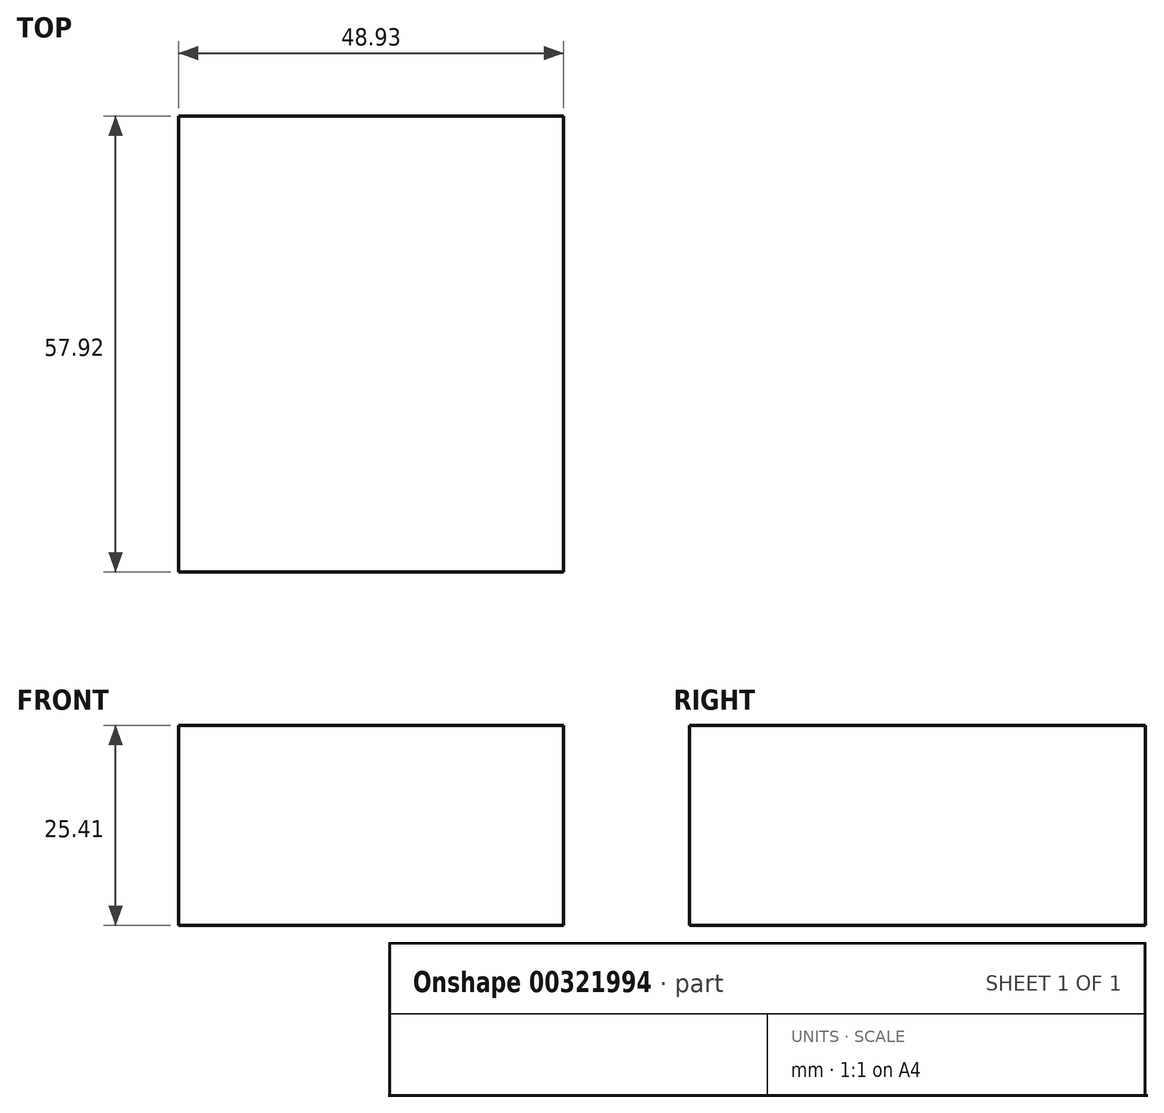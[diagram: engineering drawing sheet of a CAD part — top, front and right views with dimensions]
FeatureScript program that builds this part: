
annotation { "Feature Type Name" : "Feature", "Feature Type Description" : "" }
export const myFeature = defineFeature(function(context is Context, id is Id, definition is map)
    precondition{}
    {
        {
            var Q0;
            Q0=qCreatedBy(makeId("Front.planeOp"),FACE);
            var sketch = newSketch(context, id + "F0", { "sketchPlane" : qUnion([Q0])});
            skLineSegment(sketch, "E0.rect.bottom", {"start": v(-41.28, 9.52) * mm, "end": v(41.28, 9.52) * mm});
            skLineSegment(sketch, "E0.rect.top", {"start": v(-41.28, -9.52) * mm, "end": v(41.28, -9.52) * mm});
            skLineSegment(sketch, "E0.rect.left", {"start": v(-41.28, 9.52) * mm, "end": v(-41.28, -9.52) * mm});
            skLineSegment(sketch, "E0.rect.right", {"start": v(41.28, 9.52) * mm, "end": v(41.28, -9.52) * mm});
            skPoint(sketch, "E0.rect.middle", {"position": v(0, 0) * mm});
            skLineSegment(sketch, "E1", {"start": v(41.28, 9.52) * mm, "end": v(41.28, 27) * mm});
            skArc(sketch, "E2", {"start": v(41.28, 27) * mm, "mid": v(45.92, 38.23) * mm, "end": v(57.15, 42.88) * mm});
            skLineSegment(sketch, "E3", {"start": v(57.15, 42.88) * mm, "end": v(85.72, 42.88) * mm});
            skLineSegment(sketch, "E4.rect.bottom", {"start": v(60.32, 38.1) * mm, "end": v(111.12, 38.1) * mm});
            skLineSegment(sketch, "E4.rect.top", {"start": v(60.32, 66.68) * mm, "end": v(111.12, 66.68) * mm});
            skLineSegment(sketch, "E4.rect.left", {"start": v(60.32, 38.1) * mm, "end": v(60.32, 66.68) * mm});
            skLineSegment(sketch, "E4.rect.right", {"start": v(111.13, 38.1) * mm, "end": v(111.12, 66.68) * mm});
            skPoint(sketch, "E4.rect.middle", {"position": v(85.72, 52.39) * mm});
            skLineSegment(sketch, "E5.0", {"start": v(57.15, 61.93) * mm, "end": v(85.72, 61.93) * mm});
            skArc(sketch, "E5.1", {"start": v(22.23, 27) * mm, "mid": v(32.45, 51.7) * mm, "end": v(57.15, 61.93) * mm});
            skLineSegment(sketch, "E5.2", {"start": v(22.23, 9.52) * mm, "end": v(22.23, 27) * mm});
            skLineSegment(sketch, "E6", {"start": v(85.72, 38.1) * mm, "end": v(85.72, 66.68) * mm});
            skFitSpline(sketch, "E7", {"points": [v(-41.28, 9.53) * mm, v(57.15, 61.93) * mm], "startDerivative": vector(5.2, 92.34) * mm, "endDerivative": vector(120.92, 4.22) * mm});
            skSolve(sketch);
        }
        {
            var Q0;
            Q0=makeQuery(id+"F0.imprint","IMPRINT",FACE,{"disambiguationData":[TD([[makeQuery(id+"F0.imprint","IMPRINT",EDGE,{"derivedFrom":sQuery(id+"F0.wireOp",EDGE,"E0.rect.top")}),1.0]])]});
            extrude(context, id + "F1", {"entities" : qUnion([Q0]), "endBound" : BoundingType.SYMMETRIC, "depth" : 127 * mm});
        }
        {
            var Q0;
            {var subQ9=sQuery(id+"F0.wireOp",EDGE,"E1");Q0=makeQuery(id+"F0.imprint","IMPRINT",FACE,{"disambiguationData":[TD([[makeQuery(id+"F0.imprint","IMPRINT",EDGE,{"derivedFrom":subQ9}),1.0]])]});}
            var Q1;
            {var subQ0=sQuery(id+"F0.wireOp",EDGE,"E6");var subQ1=sQuery(id+"F0.wireOp",EDGE,"E3");var subQ2=makeQuery(id+"F0.imprint","INTERSECT",VERTEX,{"derivedFrom":[subQ1,subQ0]});Q1=makeQuery(id+"F0.imprint","IMPRINT",FACE,{"disambiguationData":[TD([[makeQuery(id+"F0.imprint","IMPRINT",EDGE,{"disambiguationData":[TD([[subQ2,1.0]])],"derivedFrom":subQ1}),1.0]])]});}
            extrude(context, id + "F2", {"entities" : qUnion([Q0, Q1]), "operationType" : NewBodyOperationType.ADD, "endBound" : BoundingType.SYMMETRIC, "depth" : 50.8 * mm});
        }
        {
            var Q0;
            {var subQ3=sQuery(id+"F0.wireOp",EDGE,"E5.2");Q0=makeQuery(id+"F0.imprint","IMPRINT",FACE,{"disambiguationData":[TD([[makeQuery(id+"F0.imprint","IMPRINT",EDGE,{"derivedFrom":subQ3}),1.0]])]});}
            extrude(context, id + "F3", {"entities" : qUnion([Q0]), "operationType" : NewBodyOperationType.ADD, "endBound" : BoundingType.SYMMETRIC, "depth" : 15.88 * mm});
        }
        {
            var Q0;
            {var subQ5=sQuery(id+"F0.wireOp",EDGE,"E4.rect.right");Q0=makeQuery(id+"F0.imprint","IMPRINT",FACE,{"disambiguationData":[TD([[makeQuery(id+"F0.imprint","IMPRINT",EDGE,{"derivedFrom":subQ5}),1.0]])]});}
            var Q1;
            Q1=sQuery(id+"F0.wireOp",EDGE,"E6");
            revolve(context, id + "F4", {"operationType" : NewBodyOperationType.ADD, "entities" : qUnion([Q0]), "axis" : qUnion([Q1]), "revolveType" : RevolveType.FULL});
        }
        {
            var Q0;
            Q0=makeQuery(id+"F1.opExtrude","CAP_EDGE",EDGE,{"disambiguationData":[OSD([sQuery(id+"F0.wireOp",EDGE,"E0.rect.right")])],"isStart":false});
            var Q1;
            Q1=makeQuery(id+"F1.opExtrude","CAP_EDGE",EDGE,{"disambiguationData":[OSD([sQuery(id+"F0.wireOp",EDGE,"E0.rect.left")])],"isStart":false});
            var Q2;
            Q2=makeQuery(id+"F1.opExtrude","CAP_EDGE",EDGE,{"disambiguationData":[OSD([sQuery(id+"F0.wireOp",EDGE,"E0.rect.right")])],"isStart":true});
            var Q3;
            Q3=makeQuery(id+"F1.opExtrude","CAP_EDGE",EDGE,{"disambiguationData":[OSD([sQuery(id+"F0.wireOp",EDGE,"E0.rect.left")])],"isStart":true});
            fillet(context, id + "F5", {"entities" : qUnion([Q0, Q1, Q2, Q3]), "radius" : 5.08 * mm, "tangentPropagation" : true, "allowEdgeOverflow" : false});
        }
        {
            var Q0;
            Q0=makeQuery(id+"F4.opRevolve","SWEPT_FACE",FACE,{"disambiguationData":[OSD([sQuery(id+"F0.wireOp",EDGE,"E4.rect.top")])]});
            var sketch = newSketch(context, id + "F6", { "sketchPlane" : qUnion([Q0])});
            skLineSegment(sketch, "E8.bottom", {"start": v(106.08, -61.94) * mm, "end": v(155, -61.94) * mm});
            skLineSegment(sketch, "E8.top", {"start": v(106.08, -119.86) * mm, "end": v(155, -119.86) * mm});
            skLineSegment(sketch, "E8.left", {"start": v(106.08, -61.94) * mm, "end": v(106.08, -119.86) * mm});
            skLineSegment(sketch, "E8.right", {"start": v(155, -61.94) * mm, "end": v(155, -119.86) * mm});
            skSolve(sketch);
        }
        {
            var Q0;
            Q0=makeQuery(id+"F6.imprint","IMPRINT",FACE,{"disambiguationData":[TD([[makeQuery(id+"F6.imprint","IMPRINT",EDGE,{"derivedFrom":sQuery(id+"F6.wireOp",EDGE,"E8.bottom")}),-1.0]])]});
            var sketch = newSketch(context, id + "F7", { "sketchPlane" : qUnion([Q0])});
            skLineSegment(sketch, "E9.0", {"start": v(106.08, -61.94) * mm, "end": v(106.08, -119.86) * mm});
            skLineSegment(sketch, "E10.0", {"start": v(106.08, -119.86) * mm, "end": v(155, -119.86) * mm});
            skLineSegment(sketch, "E11.0", {"start": v(155, -61.94) * mm, "end": v(155, -119.86) * mm});
            skLineSegment(sketch, "E12.0", {"start": v(106.08, -61.94) * mm, "end": v(155, -61.94) * mm});
            skSolve(sketch);
        }
        {
            var Q0;
            Q0=makeQuery(id+"F1.opExtrude","SWEPT_BODY",BODY,{"disambiguationData":[OSD([sQuery(id+"F0.wireOp",EDGE,"E0.rect.bottom"),sQuery(id+"F0.wireOp",EDGE,"E0.rect.top"),sQuery(id+"F0.wireOp",EDGE,"E0.rect.left"),sQuery(id+"F0.wireOp",EDGE,"E0.rect.right")])]});
            deleteBodies(context, id + "F8", {"entities" : qUnion([Q0])});
        }
        {
            var Q0;
            Q0=makeQuery(id+"F6.imprint","IMPRINT",FACE,{"disambiguationData":[TD([[makeQuery(id+"F6.imprint","IMPRINT",EDGE,{"derivedFrom":sQuery(id+"F6.wireOp",EDGE,"E8.bottom")}),-1.0]])]});
            var sketch = newSketch(context, id + "F9", { "sketchPlane" : qUnion([Q0])});
            skLineSegment(sketch, "E13.0", {"start": v(106.08, -61.94) * mm, "end": v(155, -61.94) * mm});
            skSolve(sketch);
        }
        {
            var Q0;
            Q0=sQuery(id+"F6.wireOp",EDGE,"E8.bottom");
            extrude(context, id + "F10", {"bodyType" : ToolBodyType.SURFACE, "surfaceEntities" : qUnion([Q0]), "depth" : 25.4 * mm});
        }
        {
            var Q0;
            Q0=sQuery(id+"F7.wireOp",EDGE,"E9.0");
            extrude(context, id + "F11", {"bodyType" : ToolBodyType.SURFACE, "surfaceEntities" : qUnion([Q0]), "depth" : 25.4 * mm});
        }
        {
            var Q0;
            Q0=makeQuery(id+"F9.imprint","IMPRINT",FACE,{"disambiguationData":[TD([[makeQuery(id+"F9.imprint","IMPRINT",EDGE,{"derivedFrom":sQuery(id+"F9.wireOp",EDGE,"E13.0")}),-1.0]])]});
            extrude(context, id + "F12", {"entities" : qUnion([Q0]), "depth" : 25.4 * mm});
        }
        {
            var Q0;
            Q0=makeQuery(id+"F10.opExtrude","SWEPT_BODY",BODY,{"disambiguationData":[OSD([sQuery(id+"F6.wireOp",EDGE,"E8.bottom")])]});
            deleteBodies(context, id + "F13", {"entities" : qUnion([Q0])});
        }
    });
